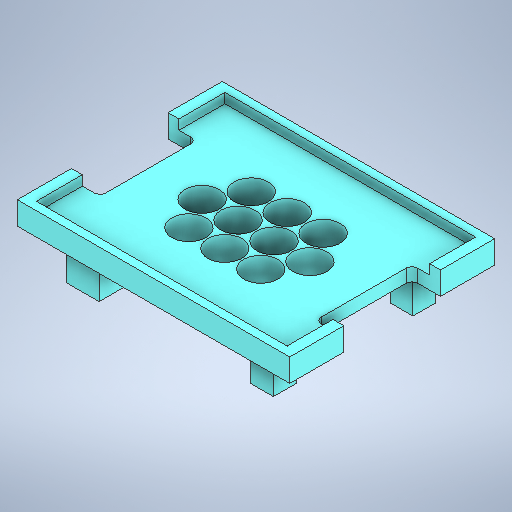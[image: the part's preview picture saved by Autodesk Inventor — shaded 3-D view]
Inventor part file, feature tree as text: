
AUTODESK INVENTOR PART (.ipt)
format: ipt  version: 2025.2 (Build 292293000, 293)  size: 902,144 bytes
history: native  units: mm
features: extrude x8, sketch x8, projected_geometry x8
ambient origin geometry x8: Origin, YZ Plane, XZ Plane, XY Plane, X Axis, Y Axis, Z Axis, Center Point
bodies: Solid1 (feature_tree)
feature tree (24):
  extrude  "Extrusion1"  Depth=21.0mm
  sketch  "Sketch4"  dims[d4=21.0mm d6=21.0mm]
  extrude  "Extrusion7"  Depth=21.0mm
  sketch  "Sketch5"  dims[d8=21.0mm d10=21.0mm]
  extrude  "Extrusion8"  Depth=21.0mm
  extrude  "Extrusion6"  Depth=21.0mm
  extrude  "Extrusion9"  Depth=15.0mm TaperAngle=0.0deg
  extrude  "Extrusion11"  Depth=21.0mm
  extrude  "Extrusion12"  Depth=0.5mm
  extrude  "Extrusion14"  Depth=0.5mm
  sketch  "Sketch1"  dims[d0=21.0mm d2=21.0mm]
  projected_geometry  "Projected Loop1"
  sketch  "Sketch6"  dims[d11=21.0mm d13=21.0mm]
  projected_geometry  "Projected Loop4"
  sketch  "Sketch7"  dims[d14=21.0mm]
  projected_geometry  "Projected Loop5"
  projected_geometry  "Projected Loop6"
  sketch  "Sketch10"  dims[d16=20.0mm d17=20.0mm d18=20.0mm d19=20.0mm d20=20.0mm d21=20.0mm d22=20.0mm d23=20.0mm d24=15.0mm d25=0.0mm]
  projected_geometry  "Projected Loop9"
  sketch  "Sketch11"  dims[d53=21.0mm d91=1.0mm]
  projected_geometry  "Projected Loop10"
  projected_geometry  "Projected Loop11"
  sketch  "Sketch13"  dims[d104=153.4mm d123=7.23mm d124=7.23mm d125=7.23mm d126=0.0mm d127=0.0mm d140=7.23mm d144=23.0mm d145=23.0mm d146=23.0mm d147=23.0mm d148=23.0mm d149=23.0mm d150=23.0mm d151=23.0mm d152=23.0mm d153=23.0mm d154=25.0mm d155=25.0mm d156=25.0mm d157=25.0mm d158=25.0mm d159=25.0mm d160=25.0mm d161=25.0mm d162=25.0mm d163=25.0mm d164=115.4mm d165=8.0mm d166=0.0mm d169=5.0mm d170=6.646447mm d171=166.692894mm d172=125.4mm d173=6.0mm d174=8.0mm d175=0.0mm d176=0.0mm d177=0.0mm d178=0.0mm d179=31.75mm d180=7.228mm d181=7.228mm d182=31.75mm d183=31.75mm d184=7.228mm d185=7.228mm d186=31.75mm d209=30.0mm d210=20.0mm d211=20.0mm d212=20.0mm d213=15.0mm d214=15.0mm d215=30.0mm d216=20.0mm d217=14.0mm d218=14.0mm d219=25.0mm d220=0.0mm d221=6.646447mm d222=70.0mm d223=0.0mm d224=30.0mm d225=30.0mm d226=20.0mm d227=20.0mm d231=10.0mm d232=0.0mm d234=0.0mm d235=0.0mm d228=0.5mm d229=0.872665mm d230=0.5mm d236=0.872665mm d237=0.5mm d238=0.872665mm]
  projected_geometry  "Projected Loop13"
